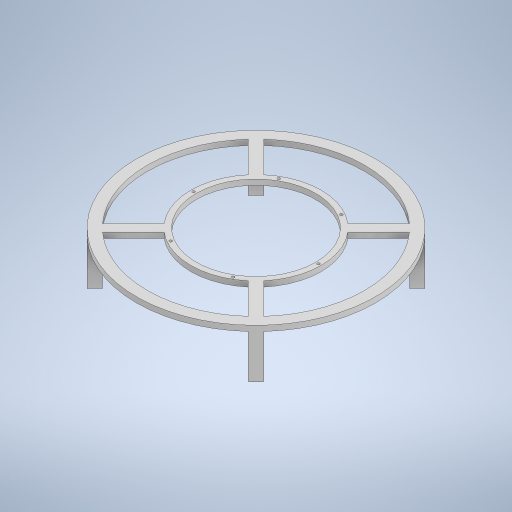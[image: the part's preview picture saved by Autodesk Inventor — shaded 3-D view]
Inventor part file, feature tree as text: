
AUTODESK INVENTOR PART (.ipt)
format: ipt  version: 2023 (Build 270158000, 158)  size: 352,768 bytes
history: native  units: in
note: dims shown in document units (in); Inventor stores cm internally (conversion verified against a paired STEP export)
features: extrude x3, sketch x2, pattern_circular x1
ambient origin geometry x8: Origin, YZ Plane, XZ Plane, XY Plane, X Axis, Y Axis, Z Axis, Center Point
bodies: Solid1 (feature_tree)
feature tree (6):
  sketch  "Sketch1"  dims[d0=20.0in d1=1.0in]
  extrude  "Extrusion1"  Depth=1.0in
  extrude  "Extrusion2"  TaperAngle=0.0deg  [1 undecoded]
  extrude  "Extrusion3"  TaperAngle=0.0deg  [1 undecoded]
  pattern_circular  "Circular Pattern1"  Angle=45.0deg  [1 undecoded]
  sketch  "Sketch2"  dims[d2=45.0deg d3=0.0in d4=0.0in d5=45.0deg d6=0.5in d7=0.5in d8=0.5in d9=0.5in d10=12.0in d11=8.0in d12=7.0in d13=0.5in d14=0.25in d15=5.75in d16=2.3622in d18=360.0deg d20=0.25in d21=3.75in d22=2.3622in d24=360.0deg d26=0.2in d27=0.5in d28=0.0in d29=4.0in d30=0.0in d31=0.5in d32=0.5in d33=7.5in d34=0.1in d35=0.0in d36=1.5748in d37=360.0deg]
note: 3 required parameter values undecoded (feature->parameter linkage not recoverable at this tier; creation-order binding heuristic only, values carry confidence <= 0.55)
